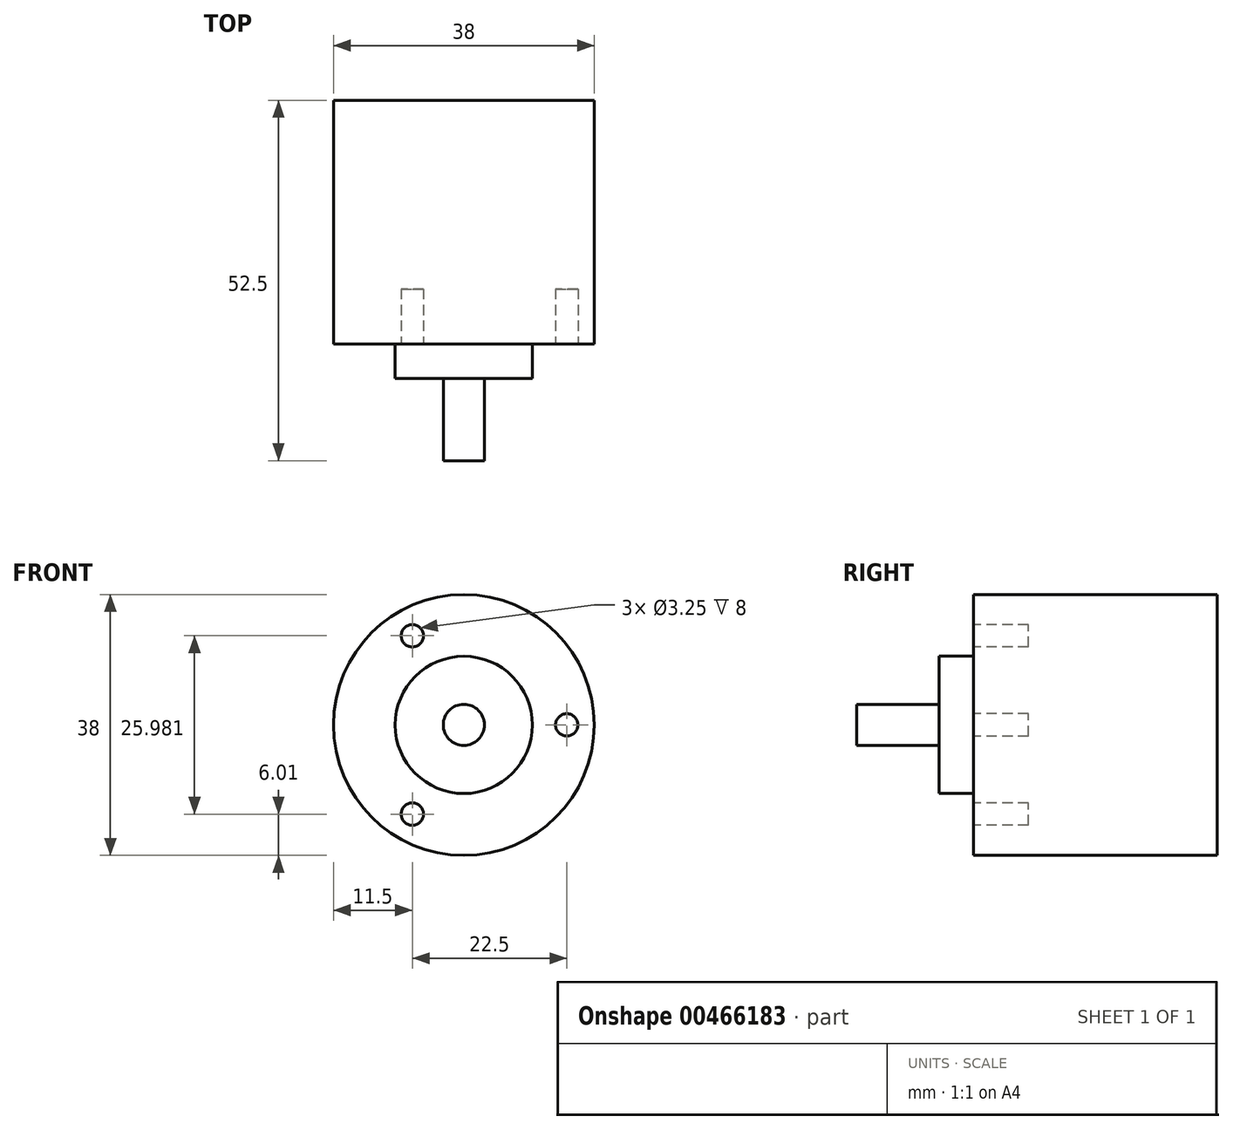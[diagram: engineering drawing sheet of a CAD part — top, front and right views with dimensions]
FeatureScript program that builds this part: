
annotation { "Feature Type Name" : "Feature", "Feature Type Description" : "" }
export const myFeature = defineFeature(function(context is Context, id is Id, definition is map)
    precondition{}
    {
        {
            var Q0;
            Q0=qCreatedBy(makeId("Front.planeOp"),FACE);
            var sketch = newSketch(context, id + "F0", { "sketchPlane" : qUnion([Q0])});
            skCircle(sketch, "E0", {"center": v(15, 0) * mm, "radius": 1.63 * mm});
            skCircle(sketch, "E1.1.0", {"center": v(-7.5, 13) * mm, "radius": 1.63 * mm});
            skCircle(sketch, "E1.2.0", {"center": v(-7.5, -13) * mm, "radius": 1.63 * mm});
            skPoint(sketch, "E1.center", {"position": v(0, 0) * mm});
            skCircle(sketch, "E2", {"center": v(0, 0) * mm, "radius": 15 * mm, "construction": true});
            skSolve(sketch);
        }
        {
            var Q0;
            Q0=qCreatedBy(makeId("Front.planeOp"),FACE);
            var sketch = newSketch(context, id + "F1", { "sketchPlane" : qUnion([Q0])});
            skCircle(sketch, "E3", {"center": v(0, 0) * mm, "radius": 19 * mm});
            skSolve(sketch);
        }
        {
            var Q0;
            Q0=makeQuery(id+"F1.imprint","IMPRINT",FACE,{"disambiguationData":[TD([[makeQuery(id+"F1.imprint","IMPRINT",EDGE,{"derivedFrom":sQuery(id+"F1.wireOp",EDGE,"E3")}),1.0]])]});
            extrude(context, id + "F2", {"entities" : qUnion([Q0]), "oppositeDirection" : true, "depth" : 35.5 * mm});
        }
        {
            var Q0;
            Q0 = qSketchRegion(id + "F0", true);
            extrude(context, id + "F3", {"entities" : qUnion([Q0]), "operationType" : NewBodyOperationType.REMOVE, "oppositeDirection" : true, "depth" : 8 * mm});
        }
        {
            var Q0;
            Q0=makeQuery(id+"F2.opExtrude","CAP_FACE",FACE,{"disambiguationData":[OSD([sQuery(id+"F1.wireOp",EDGE,"E3")])],"isStart":true});
            var sketch = newSketch(context, id + "F4", { "sketchPlane" : qUnion([Q0])});
            skCircle(sketch, "E4", {"center": v(0, 0) * mm, "radius": 10 * mm});
            skSolve(sketch);
        }
        {
            var Q0;
            Q0 = qSketchRegion(id + "F4", true);
            extrude(context, id + "F5", {"entities" : qUnion([Q0]), "operationType" : NewBodyOperationType.ADD, "depth" : 5 * mm});
        }
        {
            var Q0;
            Q0=makeQuery(id+"F5.opExtrude","CAP_FACE",FACE,{"disambiguationData":[OSD([sQuery(id+"F4.wireOp",EDGE,"E4")])],"isStart":false});
            var sketch = newSketch(context, id + "F6", { "sketchPlane" : qUnion([Q0])});
            skCircle(sketch, "E5", {"center": v(0, 0) * mm, "radius": 3 * mm});
            skSolve(sketch);
        }
        {
            var Q0;
            Q0 = qSketchRegion(id + "F6", true);
            extrude(context, id + "F7", {"entities" : qUnion([Q0]), "operationType" : NewBodyOperationType.ADD, "depth" : 12 * mm});
        }
    });
